# Revit family: Stex Winkel Universal
name_source: partatom
category: Allgemeines Modell
revit_build: Autodesk Revit 2017 (Build: 20190507_1515(x64)
units: mm (PartAtom-declared; Revit-internal decimal feet)

## family parameters
Arbeitsebenenbasiert = Ja
Beim Laden mit Abzugskörper schneiden = Nein
Bemaßung runder Anschluss = Durchmesser verwenden
Gemeinsam genutzt = Ja
Immer vertikal = Nein
Kann Basisbauteil für Bewehrung sein = Nein
Raumberechnungspunkt = Nein
Teiletyp = Normal

## types (1)
- Stex-Winkel Universal
    Anzugsmoment = 0.00 kN-m
    Artikelnummer = 127201801
    EAN = 4250928448156
    Fabrikat = MEFA
    Firma = MEFA Befestigungs- und Montagesysteme GmbH
    Gewicht = 0.22 kg
    Gewicht pro Bauteil = 0.22 kg
    Kurztext1 = Universal-Winkel 2-Loch Stex 35
    Kurztext2 = 90 ° Schenkel 47 x 47 mm
    Länge Gewinde = 0 mm  [stored 0 ft]
    Material = Stahl
    Mengeneinheit = St
    Oberflaeche = galvanisch verzinkt
    Profiltyp = 35
    Vorgabe-Ansicht = 1219 mm
    vpe = 25 St

note: [stored X ft] marks values corroborated as IEEE doubles in the binary element streams (Revit-internal decimal feet)
